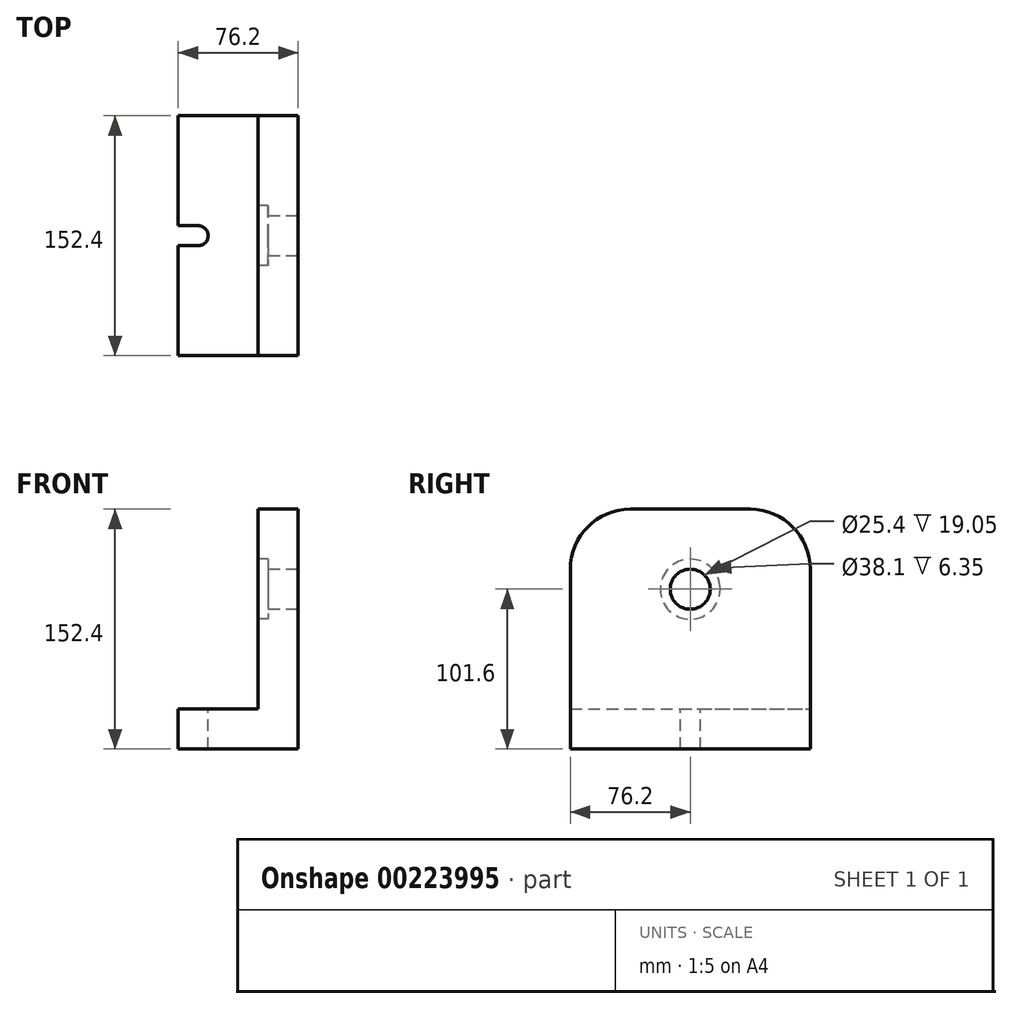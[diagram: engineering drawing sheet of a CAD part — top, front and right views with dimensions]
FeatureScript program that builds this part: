
annotation { "Feature Type Name" : "Feature", "Feature Type Description" : "" }
export const myFeature = defineFeature(function(context is Context, id is Id, definition is map)
    precondition{}
    {
        {
            var Q0;
            Q0=qCreatedBy(makeId("Front.planeOp"),FACE);
            var sketch = newSketch(context, id + "F0", { "sketchPlane" : qUnion([Q0])});
            skLineSegment(sketch, "E0", {"start": v(0, 0) * mm, "end": v(-76.2, 0) * mm});
            skLineSegment(sketch, "E1", {"start": v(-76.2, 0) * mm, "end": v(-76.2, 25.4) * mm});
            skLineSegment(sketch, "E2", {"start": v(-76.2, 25.4) * mm, "end": v(-25.4, 25.4) * mm});
            skLineSegment(sketch, "E3", {"start": v(-25.4, 25.4) * mm, "end": v(-25.4, 152.4) * mm});
            skLineSegment(sketch, "E4", {"start": v(-25.4, 152.4) * mm, "end": v(0, 152.4) * mm});
            skLineSegment(sketch, "E5", {"start": v(0, 152.4) * mm, "end": v(0, 0) * mm});
            skSolve(sketch);
        }
        {
            var Q0;
            Q0 = qSketchRegion(id + "F0", true);
            extrude(context, id + "F1", {"entities" : qUnion([Q0]), "endBound" : BoundingType.SYMMETRIC, "depth" : 152.4 * mm});
        }
        {
            var Q0;
            Q0=makeQuery(id+"F1.opExtrude","SWEPT_FACE",FACE,{"disambiguationData":[OSD([sQuery(id+"F0.wireOp",EDGE,"E5")])]});
            var sketch = newSketch(context, id + "F2", { "sketchPlane" : qUnion([Q0])});
            skCircle(sketch, "E6", {"center": v(0, 101.6) * mm, "radius": 12.7 * mm});
            skSolve(sketch);
        }
        {
            var Q0;
            Q0=makeQuery(id+"F2.imprint","IMPRINT",FACE,{"disambiguationData":[TD([[makeQuery(id+"F2.imprint","IMPRINT",EDGE,{"derivedFrom":sQuery(id+"F2.wireOp",EDGE,"E6")}),1.0]])]});
            extrude(context, id + "F3", {"entities" : qUnion([Q0]), "operationType" : NewBodyOperationType.REMOVE, "endBound" : BoundingType.THROUGH_ALL, "oppositeDirection" : true, "depth" : 25.4 * mm});
        }
        {
            var Q0;
            Q0=makeQuery(id+"F1.opExtrude","SWEPT_FACE",FACE,{"disambiguationData":[OSD([sQuery(id+"F0.wireOp",EDGE,"E2")])]});
            var sketch = newSketch(context, id + "F4", { "sketchPlane" : qUnion([Q0])});
            skCircle(sketch, "E7", {"center": v(-63.5, 0) * mm, "radius": 6.35 * mm});
            skLineSegment(sketch, "E8", {"start": v(-63.5, 6.35) * mm, "end": v(-76.2, 6.35) * mm});
            skLineSegment(sketch, "E9", {"start": v(-63.5, -6.35) * mm, "end": v(-76.2, -6.35) * mm});
            skSolve(sketch);
        }
        {
            var Q0;
            Q0 = qSketchRegion(id + "F4", true);
            var Q1;
            {var subQ0=sQuery(id+"F4.wireOp",EDGE,"E8");Q1=makeQuery(id+"F4.imprint","IMPRINT",FACE,{"disambiguationData":[TD([[makeQuery(id+"F4.imprint","IMPRINT",EDGE,{"derivedFrom":subQ0}),1.0]])]});}
            extrude(context, id + "F5", {"entities" : qUnion([Q0, Q1]), "operationType" : NewBodyOperationType.REMOVE, "endBound" : BoundingType.THROUGH_ALL, "oppositeDirection" : true, "depth" : 25.4 * mm});
        }
        {
            var Q0;
            Q0=makeQuery(id+"F1.opExtrude","CAP_EDGE",EDGE,{"disambiguationData":[OSD([sQuery(id+"F0.wireOp",EDGE,"E4")])],"isStart":false});
            var Q1;
            Q1=makeQuery(id+"F1.opExtrude","CAP_EDGE",EDGE,{"disambiguationData":[OSD([sQuery(id+"F0.wireOp",EDGE,"E4")])],"isStart":true});
            fillet(context, id + "F6", {"entities" : qUnion([Q0, Q1]), "radius" : 38.1 * mm, "tangentPropagation" : true, "allowEdgeOverflow" : false});
        }
        {
            var Q0;
            Q0=makeQuery(id+"F1.opExtrude","SWEPT_FACE",FACE,{"disambiguationData":[OSD([sQuery(id+"F0.wireOp",EDGE,"E3")])]});
            var sketch = newSketch(context, id + "F7", { "sketchPlane" : qUnion([Q0])});
            skCircle(sketch, "E10", {"center": v(0, 101.6) * mm, "radius": 19.05 * mm});
            skSolve(sketch);
        }
        {
            var Q0;
            Q0 = qSketchRegion(id + "F7", true);
            extrude(context, id + "F8", {"entities" : qUnion([Q0]), "operationType" : NewBodyOperationType.REMOVE, "oppositeDirection" : true, "depth" : 6.35 * mm});
        }
    });
